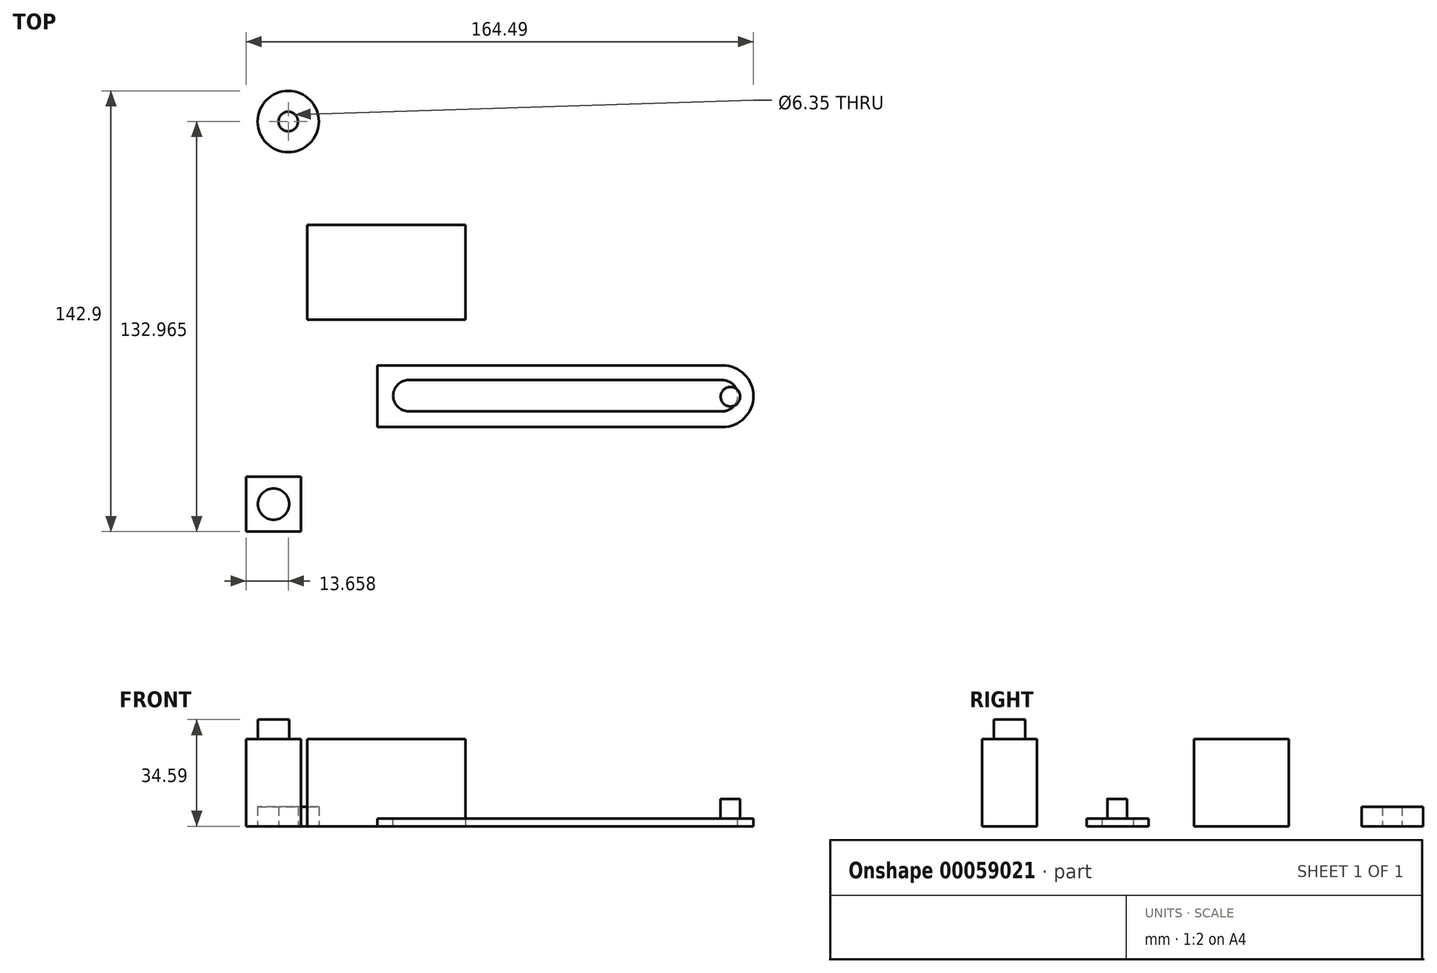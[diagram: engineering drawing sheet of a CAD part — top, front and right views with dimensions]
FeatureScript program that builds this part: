
annotation { "Feature Type Name" : "Feature", "Feature Type Description" : "" }
export const myFeature = defineFeature(function(context is Context, id is Id, definition is map)
    precondition{}
    {
        {
            var Q0;
            Q0=qCreatedBy(makeId("Top.planeOp"),FACE);
            var sketch = newSketch(context, id + "F0", { "sketchPlane" : qUnion([Q0])});
            skLineSegment(sketch, "E0.bottom", {"start": v(0, 0) * mm, "end": v(-51.3, 0) * mm});
            skLineSegment(sketch, "E0.top", {"start": v(0, 30.78) * mm, "end": v(-51.3, 30.78) * mm});
            skLineSegment(sketch, "E0.left", {"start": v(0, 0) * mm, "end": v(0, 30.78) * mm});
            skLineSegment(sketch, "E0.right", {"start": v(-51.3, 0) * mm, "end": v(-51.3, 30.78) * mm});
            skSolve(sketch);
        }
        {
            var Q0;
            Q0=qSketchRegion(id+"F0",true);
            extrude(context, id + "F1", {"entities" : qUnion([Q0]), "depth" : 28.24 * mm});
        }
        {
            var Q0;
            Q0=qCreatedBy(makeId("Top.planeOp"),FACE);
            var sketch = newSketch(context, id + "F2", { "sketchPlane" : qUnion([Q0])});
            skCircle(sketch, "E1", {"center": v(-57.52, 64.3) * mm, "radius": 9.93 * mm});
            skCircle(sketch, "E2", {"center": v(-57.52, 64.3) * mm, "radius": 3.18 * mm});
            skSolve(sketch);
        }
        {
            var Q0;
            Q0=qSketchRegion(id+"F2",true);
            extrude(context, id + "F3", {"entities" : qUnion([Q0]), "depth" : 6.35 * mm});
        }
        {
            var Q0;
            Q0=qCreatedBy(makeId("Top.planeOp"),FACE);
            var sketch = newSketch(context, id + "F4", { "sketchPlane" : qUnion([Q0])});
            skLineSegment(sketch, "E3.bottom", {"start": v(-71.18, -68.66) * mm, "end": v(-53.4, -68.66) * mm});
            skLineSegment(sketch, "E3.top", {"start": v(-71.18, -50.88) * mm, "end": v(-53.4, -50.88) * mm});
            skLineSegment(sketch, "E3.left", {"start": v(-71.18, -68.66) * mm, "end": v(-71.18, -50.88) * mm});
            skLineSegment(sketch, "E3.right", {"start": v(-53.4, -68.66) * mm, "end": v(-53.4, -50.88) * mm});
            skSolve(sketch);
        }
        {
            var Q0;
            Q0=qSketchRegion(id+"F4",true);
            extrude(context, id + "F5", {"entities" : qUnion([Q0]), "depth" : 28.24 * mm});
        }
        {
            var Q0;
            Q0=qCreatedBy(makeId("Top.planeOp"),FACE);
            var sketch = newSketch(context, id + "F6", { "sketchPlane" : qUnion([Q0])});
            skLineSegment(sketch, "E4.bottom", {"start": v(83.31, -14.78) * mm, "end": v(-28.69, -14.78) * mm});
            skLineSegment(sketch, "E4.top", {"start": v(83.31, -34.78) * mm, "end": v(-28.69, -34.78) * mm});
            skLineSegment(sketch, "E4.left", {"start": v(83.31, -14.78) * mm, "end": v(83.31, -34.78) * mm});
            skLineSegment(sketch, "E4.right", {"start": v(-28.69, -14.78) * mm, "end": v(-28.69, -34.78) * mm});
            skArc(sketch, "E5", {"start": v(83.31, -34.78) * mm, "mid": v(93.31, -24.78) * mm, "end": v(83.31, -14.78) * mm});
            skSolve(sketch);
        }
        {
            var Q0;
            Q0=qSketchRegion(id+"F6",true);
            extrude(context, id + "F7", {"entities" : qUnion([Q0]), "depth" : 2.54 * mm});
        }
        {
            var Q0;
            Q0=makeQuery(id+"F7.opExtrude","CAP_FACE",FACE,{"disambiguationData":[OSD([sQuery(id+"F6.wireOp",EDGE,"E4.bottom"),sQuery(id+"F6.wireOp",EDGE,"E4.top"),sQuery(id+"F6.wireOp",EDGE,"E4.left"),sQuery(id+"F6.wireOp",EDGE,"E4.right")])],"isStart":false});
            var sketch = newSketch(context, id + "F8", { "sketchPlane" : qUnion([Q0])});
            skLineSegment(sketch, "E6.bottom", {"start": v(-18.41, -19.54) * mm, "end": v(83.19, -19.54) * mm});
            skLineSegment(sketch, "E6.top", {"start": v(-18.41, -29.7) * mm, "end": v(83.19, -29.7) * mm});
            skLineSegment(sketch, "E6.left", {"start": v(-18.41, -19.54) * mm, "end": v(-18.41, -29.7) * mm});
            skLineSegment(sketch, "E6.right", {"start": v(83.19, -19.54) * mm, "end": v(83.19, -29.7) * mm});
            skSolve(sketch);
        }
        {
            var Q0;
            Q0=qSketchRegion(id+"F8",true);
            extrude(context, id + "F9", {"entities" : qUnion([Q0]), "operationType" : NewBodyOperationType.REMOVE, "endBound" : BoundingType.THROUGH_ALL, "oppositeDirection" : true, "depth" : 25.4 * mm});
        }
        {
            var Q0;
            Q0=makeQuery(id+"F7.opExtrude","CAP_FACE",FACE,{"disambiguationData":[OSD([sQuery(id+"F6.wireOp",EDGE,"E4.bottom"),sQuery(id+"F6.wireOp",EDGE,"E4.top"),sQuery(id+"F6.wireOp",EDGE,"E4.left"),sQuery(id+"F6.wireOp",EDGE,"E4.right")])],"isStart":false});
            var sketch = newSketch(context, id + "F10", { "sketchPlane" : qUnion([Q0])});
            skCircle(sketch, "E7", {"center": v(83.19, -24.62) * mm, "radius": 5.08 * mm});
            skCircle(sketch, "E8", {"center": v(-18.41, -24.62) * mm, "radius": 5.08 * mm});
            skSolve(sketch);
        }
        {
            var Q0;
            Q0=qSketchRegion(id+"F10",true);
            extrude(context, id + "F11", {"entities" : qUnion([Q0]), "operationType" : NewBodyOperationType.REMOVE, "endBound" : BoundingType.THROUGH_ALL, "oppositeDirection" : true, "depth" : 25.4 * mm});
        }
        {
            var Q0;
            Q0=makeQuery(id+"F5.opExtrude","CAP_FACE",FACE,{"disambiguationData":[OSD([sQuery(id+"F4.wireOp",EDGE,"E3.bottom"),sQuery(id+"F4.wireOp",EDGE,"E3.top"),sQuery(id+"F4.wireOp",EDGE,"E3.left"),sQuery(id+"F4.wireOp",EDGE,"E3.right")])],"isStart":false});
            var sketch = newSketch(context, id + "F12", { "sketchPlane" : qUnion([Q0])});
            skCircle(sketch, "E9", {"center": v(-62.3, -59.77) * mm, "radius": 5.08 * mm});
            skSolve(sketch);
        }
        {
            var Q0;
            Q0=qSketchRegion(id+"F12",true);
            extrude(context, id + "F13", {"entities" : qUnion([Q0]), "operationType" : NewBodyOperationType.ADD, "depth" : 6.35 * mm});
        }
        {
            var Q0;
            Q0=makeQuery(id+"F7.opExtrude","CAP_FACE",FACE,{"disambiguationData":[OSD([sQuery(id+"F6.wireOp",EDGE,"E4.bottom"),sQuery(id+"F6.wireOp",EDGE,"E4.top"),sQuery(id+"F6.wireOp",EDGE,"E4.right"),sQuery(id+"F6.wireOp",EDGE,"E5")])],"isStart":false});
            var sketch = newSketch(context, id + "F14", { "sketchPlane" : qUnion([Q0])});
            skCircle(sketch, "E10", {"center": v(85.85, -24.94) * mm, "radius": 3.18 * mm});
            skSolve(sketch);
        }
        {
            var Q0;
            Q0=qSketchRegion(id+"F14",true);
            extrude(context, id + "F15", {"entities" : qUnion([Q0]), "operationType" : NewBodyOperationType.ADD, "depth" : 6.35 * mm});
        }
        {
            var Q0;
            Q0=qSketchRegion(id+"F2",true);
            extrude(context, id + "F16", {"entities" : qUnion([Q0]), "operationType" : NewBodyOperationType.REMOVE, "oppositeDirection" : true, "depth" : 25.4 * mm});
        }
    });
